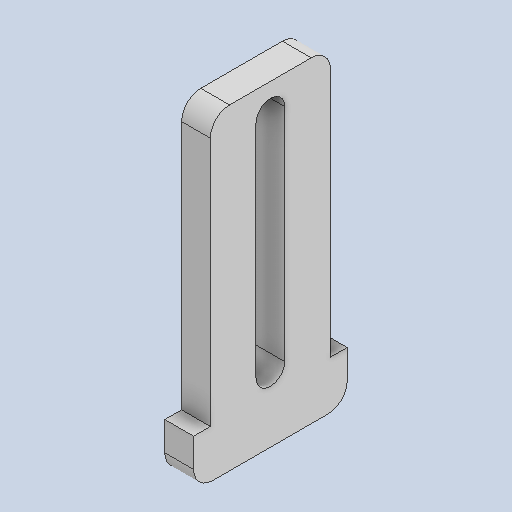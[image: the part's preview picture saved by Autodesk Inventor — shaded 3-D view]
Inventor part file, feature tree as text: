
AUTODESK INVENTOR PART (.ipt)
format: ipt  version: 2023 (Build 270158000, 158)  size: 129,536 bytes
history: native  units: mm
features: extrude x1, sketch x1
ambient origin geometry x8: Origin, YZ Plane, XZ Plane, XY Plane, X Axis, Y Axis, Z Axis, Center Point
bodies: Body1 (feature_tree)
feature tree (2):
  extrude  "Extrusion3"  Depth=5.0mm
  sketch  "Sketch1"  dims[d1=16.0mm d2=6.0mm d3=1.75mm d5=2.0mm d14=1.75mm d18=3.0mm d19=3.0mm d21=2.0mm d22=3.0mm d23=0.0mm d24=28.0mm d25=2.0mm d26=5.0mm]
